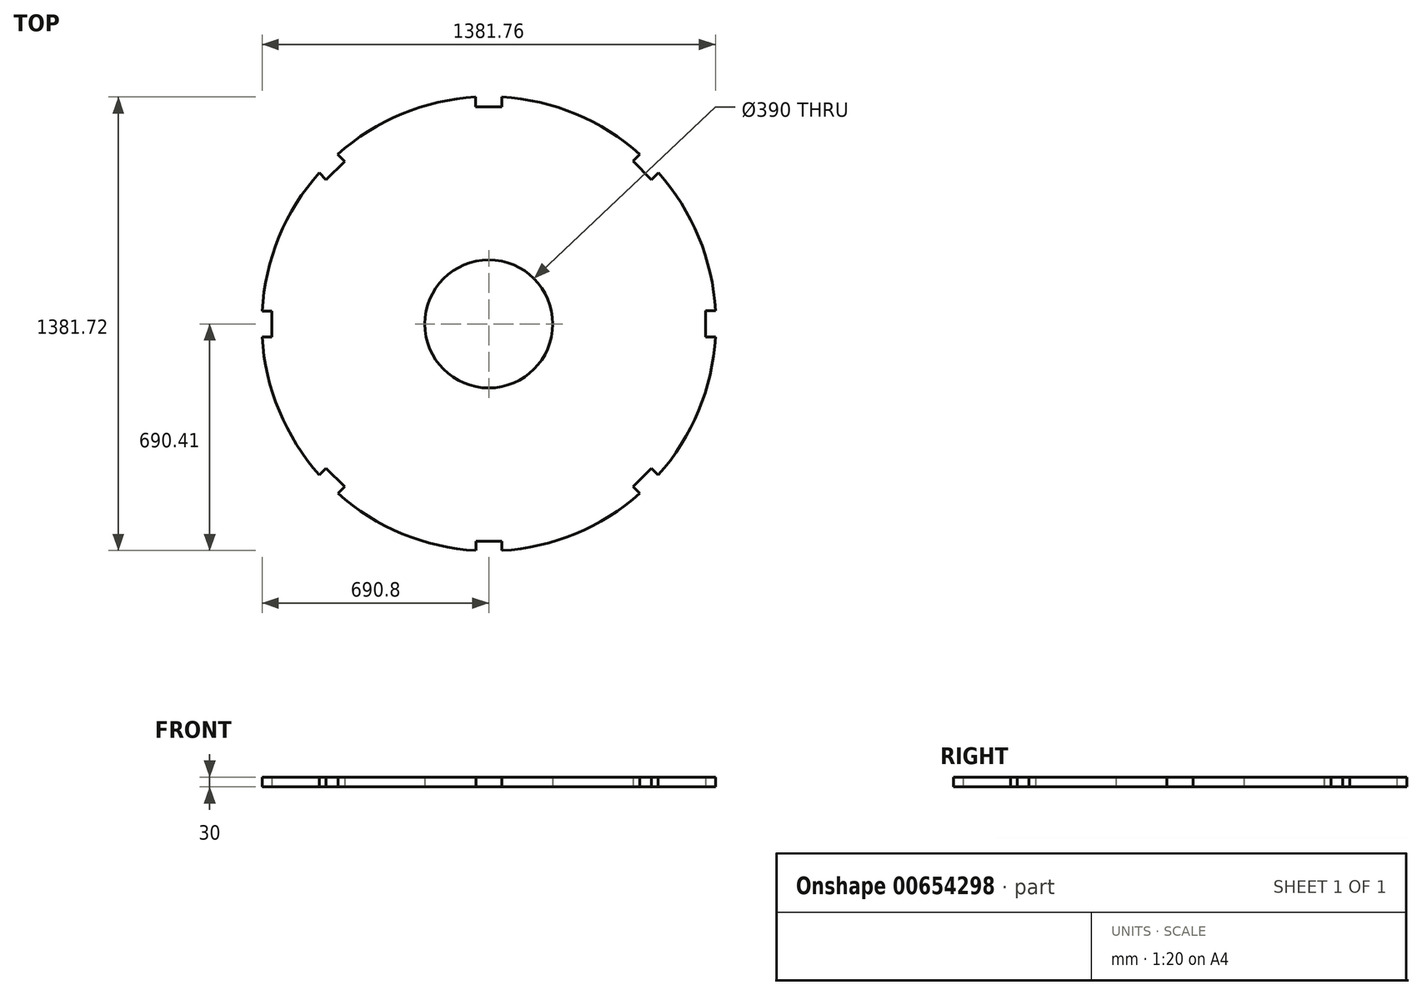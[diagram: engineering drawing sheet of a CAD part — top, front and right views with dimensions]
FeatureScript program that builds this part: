
annotation { "Feature Type Name" : "Feature", "Feature Type Description" : "" }
export const myFeature = defineFeature(function(context is Context, id is Id, definition is map)
    precondition{}
    {
        {
            var Q0;
            Q0=qCreatedBy(makeId("Top.planeOp"),FACE);
            var sketch = newSketch(context, id + "F0", { "sketchPlane" : qUnion([Q0])});
            skArc(sketch, "E0", {"start": v(-39.91, 691.29) * mm, "mid": v(-265.05, 639.64) * mm, "end": v(-460.64, 516.77) * mm});
            skCircle(sketch, "E1", {"center": v(0, 0) * mm, "radius": 195 * mm});
            skLineSegment(sketch, "E2", {"start": v(0.09, 0.45) * mm, "end": v(0.09, 661.31) * mm});
            skLineSegment(sketch, "E3.0", {"start": v(-39.91, 0.45) * mm, "end": v(-39.91, 190.87) * mm});
            skLineSegment(sketch, "E4", {"start": v(39.7, 691.31) * mm, "end": v(39.7, 661.31) * mm});
            skLineSegment(sketch, "E5", {"start": v(39.7, 661.31) * mm, "end": v(-39.91, 661.31) * mm});
            skLineSegment(sketch, "E6.trimOffspring", {"start": v(-39.91, 661.31) * mm, "end": v(-39.91, 692.45) * mm});
            skLineSegment(sketch, "E7.1.0", {"start": v(-495.84, 439.4) * mm, "end": v(-517.85, 461.41) * mm});
            skLineSegment(sketch, "E7.1.1", {"start": v(-460.77, 516.9) * mm, "end": v(-439.55, 495.68) * mm});
            skLineSegment(sketch, "E7.1.2", {"start": v(-439.55, 495.68) * mm, "end": v(-495.84, 439.4) * mm});
            skLineSegment(sketch, "E7.1.3", {"start": v(-460.77, 516.9) * mm, "end": v(-439.55, 495.68) * mm});
            skLineSegment(sketch, "E7.1.4", {"start": v(-495.84, 439.4) * mm, "end": v(-517.85, 461.41) * mm});
            skLineSegment(sketch, "E7.1.5", {"start": v(-439.55, 495.68) * mm, "end": v(-495.84, 439.4) * mm});
            skLineSegment(sketch, "E7.1.6", {"start": v(-460.77, 516.9) * mm, "end": v(-439.55, 495.68) * mm});
            skLineSegment(sketch, "E7.1.7", {"start": v(-439.55, 495.68) * mm, "end": v(-495.84, 439.4) * mm});
            skLineSegment(sketch, "E7.1.8", {"start": v(-495.84, 439.4) * mm, "end": v(-517.85, 461.41) * mm});
            skLineSegment(sketch, "E7.1.9", {"start": v(-439.55, 495.68) * mm, "end": v(-495.84, 439.4) * mm});
            skLineSegment(sketch, "E7.1.10", {"start": v(-460.77, 516.9) * mm, "end": v(-439.55, 495.68) * mm});
            skLineSegment(sketch, "E7.1.11", {"start": v(-495.84, 439.4) * mm, "end": v(-517.85, 461.41) * mm});
            skLineSegment(sketch, "E7.2.0", {"start": v(-661.31, -39.91) * mm, "end": v(-692.45, -39.91) * mm});
            skLineSegment(sketch, "E7.2.1", {"start": v(-691.31, 39.7) * mm, "end": v(-661.31, 39.7) * mm});
            skLineSegment(sketch, "E7.2.2", {"start": v(-661.31, 39.7) * mm, "end": v(-661.31, -39.91) * mm});
            skLineSegment(sketch, "E7.2.3", {"start": v(-691.31, 39.7) * mm, "end": v(-661.31, 39.7) * mm});
            skLineSegment(sketch, "E7.2.4", {"start": v(-661.31, -39.91) * mm, "end": v(-692.45, -39.91) * mm});
            skLineSegment(sketch, "E7.2.5", {"start": v(-661.31, 39.7) * mm, "end": v(-661.31, -39.91) * mm});
            skLineSegment(sketch, "E7.2.6", {"start": v(-691.31, 39.7) * mm, "end": v(-661.31, 39.7) * mm});
            skLineSegment(sketch, "E7.2.7", {"start": v(-661.31, 39.7) * mm, "end": v(-661.31, -39.91) * mm});
            skLineSegment(sketch, "E7.2.8", {"start": v(-661.31, -39.91) * mm, "end": v(-692.45, -39.91) * mm});
            skLineSegment(sketch, "E7.2.9", {"start": v(-661.31, 39.7) * mm, "end": v(-661.31, -39.91) * mm});
            skLineSegment(sketch, "E7.2.10", {"start": v(-691.31, 39.7) * mm, "end": v(-661.31, 39.7) * mm});
            skLineSegment(sketch, "E7.2.11", {"start": v(-661.31, -39.91) * mm, "end": v(-692.45, -39.91) * mm});
            skLineSegment(sketch, "E7.3.0", {"start": v(-439.4, -495.84) * mm, "end": v(-461.41, -517.85) * mm});
            skLineSegment(sketch, "E7.3.1", {"start": v(-516.9, -460.77) * mm, "end": v(-495.68, -439.55) * mm});
            skLineSegment(sketch, "E7.3.2", {"start": v(-495.68, -439.55) * mm, "end": v(-439.4, -495.84) * mm});
            skLineSegment(sketch, "E7.3.3", {"start": v(-516.9, -460.77) * mm, "end": v(-495.68, -439.55) * mm});
            skLineSegment(sketch, "E7.3.4", {"start": v(-439.4, -495.84) * mm, "end": v(-461.41, -517.85) * mm});
            skLineSegment(sketch, "E7.3.5", {"start": v(-495.68, -439.55) * mm, "end": v(-439.4, -495.84) * mm});
            skLineSegment(sketch, "E7.3.6", {"start": v(-516.9, -460.77) * mm, "end": v(-495.68, -439.55) * mm});
            skLineSegment(sketch, "E7.3.7", {"start": v(-495.68, -439.55) * mm, "end": v(-439.4, -495.84) * mm});
            skLineSegment(sketch, "E7.3.8", {"start": v(-439.4, -495.84) * mm, "end": v(-461.41, -517.85) * mm});
            skLineSegment(sketch, "E7.3.9", {"start": v(-495.68, -439.55) * mm, "end": v(-439.4, -495.84) * mm});
            skLineSegment(sketch, "E7.3.10", {"start": v(-516.9, -460.77) * mm, "end": v(-495.68, -439.55) * mm});
            skLineSegment(sketch, "E7.3.11", {"start": v(-439.4, -495.84) * mm, "end": v(-461.41, -517.85) * mm});
            skLineSegment(sketch, "E8.1.4.0", {"start": v(39.91, -661.31) * mm, "end": v(39.91, -692.45) * mm});
            skLineSegment(sketch, "E8.3.4.0", {"start": v(-39.7, -691.31) * mm, "end": v(-39.7, -661.31) * mm});
            skLineSegment(sketch, "E8.6.4.0", {"start": v(-39.7, -661.31) * mm, "end": v(39.91, -661.31) * mm});
            skLineSegment(sketch, "E8.9.4.0", {"start": v(-39.7, -691.31) * mm, "end": v(-39.7, -661.31) * mm});
            skLineSegment(sketch, "E8.12.4.0", {"start": v(39.91, -661.31) * mm, "end": v(39.91, -692.45) * mm});
            skLineSegment(sketch, "E8.15.4.0", {"start": v(-39.7, -661.31) * mm, "end": v(39.91, -661.31) * mm});
            skLineSegment(sketch, "E8.18.4.0", {"start": v(-39.7, -691.31) * mm, "end": v(-39.7, -661.31) * mm});
            skLineSegment(sketch, "E8.21.4.0", {"start": v(-39.7, -661.31) * mm, "end": v(39.91, -661.31) * mm});
            skLineSegment(sketch, "E8.24.4.0", {"start": v(39.91, -661.31) * mm, "end": v(39.91, -692.45) * mm});
            skLineSegment(sketch, "E8.27.4.0", {"start": v(-39.7, -661.31) * mm, "end": v(39.91, -661.31) * mm});
            skLineSegment(sketch, "E8.30.4.0", {"start": v(-39.7, -691.31) * mm, "end": v(-39.7, -661.31) * mm});
            skLineSegment(sketch, "E8.33.4.0", {"start": v(39.91, -661.31) * mm, "end": v(39.91, -692.45) * mm});
            skLineSegment(sketch, "E8.1.5.0", {"start": v(495.84, -439.4) * mm, "end": v(517.85, -461.41) * mm});
            skLineSegment(sketch, "E8.3.5.0", {"start": v(460.77, -516.9) * mm, "end": v(439.55, -495.68) * mm});
            skLineSegment(sketch, "E8.6.5.0", {"start": v(439.55, -495.68) * mm, "end": v(495.84, -439.4) * mm});
            skLineSegment(sketch, "E8.9.5.0", {"start": v(460.77, -516.9) * mm, "end": v(439.55, -495.68) * mm});
            skLineSegment(sketch, "E8.12.5.0", {"start": v(495.84, -439.4) * mm, "end": v(517.85, -461.41) * mm});
            skLineSegment(sketch, "E8.15.5.0", {"start": v(439.55, -495.68) * mm, "end": v(495.84, -439.4) * mm});
            skLineSegment(sketch, "E8.18.5.0", {"start": v(460.77, -516.9) * mm, "end": v(439.55, -495.68) * mm});
            skLineSegment(sketch, "E8.21.5.0", {"start": v(439.55, -495.68) * mm, "end": v(495.84, -439.4) * mm});
            skLineSegment(sketch, "E8.24.5.0", {"start": v(495.84, -439.4) * mm, "end": v(517.85, -461.41) * mm});
            skLineSegment(sketch, "E8.27.5.0", {"start": v(439.55, -495.68) * mm, "end": v(495.84, -439.4) * mm});
            skLineSegment(sketch, "E8.30.5.0", {"start": v(460.77, -516.9) * mm, "end": v(439.55, -495.68) * mm});
            skLineSegment(sketch, "E8.33.5.0", {"start": v(495.84, -439.4) * mm, "end": v(517.85, -461.41) * mm});
            skLineSegment(sketch, "E8.1.6.0", {"start": v(661.31, 39.91) * mm, "end": v(692.45, 39.91) * mm});
            skLineSegment(sketch, "E8.3.6.0", {"start": v(691.31, -39.7) * mm, "end": v(661.31, -39.7) * mm});
            skLineSegment(sketch, "E8.6.6.0", {"start": v(661.31, -39.7) * mm, "end": v(661.31, 39.91) * mm});
            skLineSegment(sketch, "E8.9.6.0", {"start": v(691.31, -39.7) * mm, "end": v(661.31, -39.7) * mm});
            skLineSegment(sketch, "E8.12.6.0", {"start": v(661.31, 39.91) * mm, "end": v(692.45, 39.91) * mm});
            skLineSegment(sketch, "E8.15.6.0", {"start": v(661.31, -39.7) * mm, "end": v(661.31, 39.91) * mm});
            skLineSegment(sketch, "E8.18.6.0", {"start": v(691.31, -39.7) * mm, "end": v(661.31, -39.7) * mm});
            skLineSegment(sketch, "E8.21.6.0", {"start": v(661.31, -39.7) * mm, "end": v(661.31, 39.91) * mm});
            skLineSegment(sketch, "E8.24.6.0", {"start": v(661.31, 39.91) * mm, "end": v(692.45, 39.91) * mm});
            skLineSegment(sketch, "E8.27.6.0", {"start": v(661.31, -39.7) * mm, "end": v(661.31, 39.91) * mm});
            skLineSegment(sketch, "E8.30.6.0", {"start": v(691.31, -39.7) * mm, "end": v(661.31, -39.7) * mm});
            skLineSegment(sketch, "E8.33.6.0", {"start": v(661.31, 39.91) * mm, "end": v(692.45, 39.91) * mm});
            skLineSegment(sketch, "E8.1.7.0", {"start": v(439.4, 495.84) * mm, "end": v(461.41, 517.85) * mm});
            skLineSegment(sketch, "E8.3.7.0", {"start": v(516.9, 460.77) * mm, "end": v(495.68, 439.55) * mm});
            skLineSegment(sketch, "E8.6.7.0", {"start": v(495.68, 439.55) * mm, "end": v(439.4, 495.84) * mm});
            skLineSegment(sketch, "E8.9.7.0", {"start": v(516.9, 460.77) * mm, "end": v(495.68, 439.55) * mm});
            skLineSegment(sketch, "E8.12.7.0", {"start": v(439.4, 495.84) * mm, "end": v(461.41, 517.85) * mm});
            skLineSegment(sketch, "E8.15.7.0", {"start": v(495.68, 439.55) * mm, "end": v(439.4, 495.84) * mm});
            skLineSegment(sketch, "E8.18.7.0", {"start": v(516.9, 460.77) * mm, "end": v(495.68, 439.55) * mm});
            skLineSegment(sketch, "E8.21.7.0", {"start": v(495.68, 439.55) * mm, "end": v(439.4, 495.84) * mm});
            skLineSegment(sketch, "E8.24.7.0", {"start": v(439.4, 495.84) * mm, "end": v(461.41, 517.85) * mm});
            skLineSegment(sketch, "E8.27.7.0", {"start": v(495.68, 439.55) * mm, "end": v(439.4, 495.84) * mm});
            skLineSegment(sketch, "E8.30.7.0", {"start": v(516.9, 460.77) * mm, "end": v(495.68, 439.55) * mm});
            skLineSegment(sketch, "E8.33.7.0", {"start": v(439.4, 495.84) * mm, "end": v(461.41, 517.85) * mm});
            skArc(sketch, "E9.trimOffspring", {"start": v(460.56, 517) * mm, "mid": v(264.88, 639.78) * mm, "end": v(39.7, 691.31) * mm});
            skArc(sketch, "E10.trimOffspring", {"start": v(690.96, 39.91) * mm, "mid": v(639.5, 265.04) * mm, "end": v(516.84, 460.7) * mm});
            skArc(sketch, "E11.trimOffspring", {"start": v(516.56, -460.12) * mm, "mid": v(639.3, -264.65) * mm, "end": v(690.92, -39.7) * mm});
            skArc(sketch, "E12.trimOffspring", {"start": v(39.91, -690.4) * mm, "mid": v(264.8, -638.93) * mm, "end": v(460.25, -516.38) * mm});
            skArc(sketch, "E13.trimOffspring", {"start": v(-460, -516.45) * mm, "mid": v(-264.55, -638.95) * mm, "end": v(-39.7, -690.4) * mm});
            skArc(sketch, "E14.trimOffspring", {"start": v(-690.73, -39.91) * mm, "mid": v(-639.06, -264.8) * mm, "end": v(-516.32, -460.19) * mm});
            skArc(sketch, "E15.trimOffspring", {"start": v(-516.89, 460.45) * mm, "mid": v(-639.44, 264.78) * mm, "end": v(-690.8, 39.7) * mm});
            skSolve(sketch);
        }
        {
            var Q0;
            Q0 = qSketchRegion(id + "F0", true);
            extrude(context, id + "F1", {"entities" : qUnion([Q0]), "depth" : 30 * mm, "offsetDistance" : 25 * mm});
        }
    });
